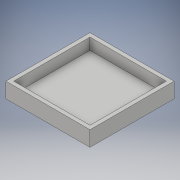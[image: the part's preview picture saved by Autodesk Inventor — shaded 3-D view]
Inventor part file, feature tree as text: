
AUTODESK INVENTOR PART (.ipt)
format: ipt  version: 2018 (Build 220112000, 112)  size: 109,568 bytes
history: native  units: mm
features: extrude x2, sketch x2
ambient origin geometry x8: Origin, YZ Plane, XZ Plane, XY Plane, X Axis, Y Axis, Z Axis, Center Point
bodies: Solid1 (feature_tree)
feature tree (4):
  extrude  "Extrusion1"  Depth=20.0mm
  extrude  "Extrusion2"  Depth=22.0mm
  sketch  "Sketch1"  dims[d0=20.0mm d1=20.0mm]
  sketch  "Sketch2"  dims[d2=22.0mm d3=22.0mm d4=1.0mm d5=1.0mm d6=3.0mm d7=0.0mm d8=1.0mm d9=0.0mm]
